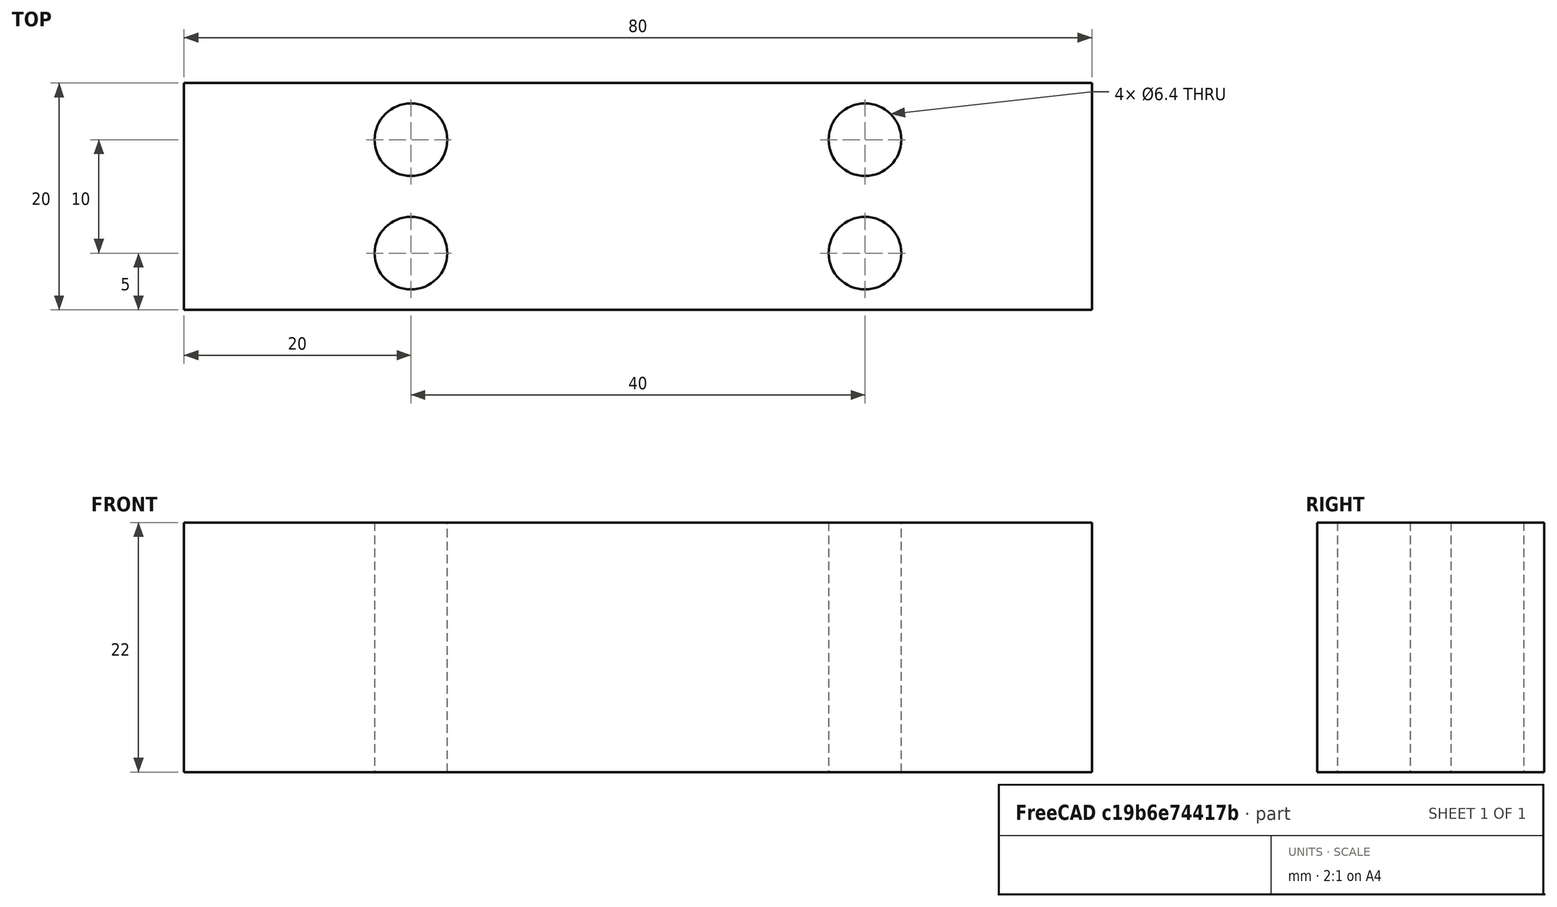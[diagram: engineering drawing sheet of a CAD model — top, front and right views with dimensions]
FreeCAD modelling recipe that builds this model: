
FCSTD DOCUMENT  (FreeCAD 0.18R16110 (Git))
Label: nutblock1b
License: All rights reserved
LicenseURL: http://en.wikipedia.org/wiki/All_rights_reserved
objects: Sketcher::SketchObject×1, PartDesign::Pad×1, PartDesign::Body×1
note: 4 computed .brp shape members not serialized (recipe doc carries the construction recipe); baked Part::Feature solids carry a one-line shape summary decoded from their .brp

FEATURE [Sketcher::SketchObject] Sketch
  MapMode = 5
  Support = -> [XY_Plane]
  sketch-geometry (8):
    g0: LineSegment StartX=0 StartY=20 StartZ=0 EndX=80 EndY=20 EndZ=0
    g1: LineSegment StartX=80 StartY=20 StartZ=0 EndX=80 EndY=0 EndZ=0
    g2: LineSegment StartX=80 StartY=0 StartZ=0 EndX=0 EndY=0 EndZ=0
    g3: LineSegment StartX=0 StartY=0 StartZ=0 EndX=0 EndY=20 EndZ=0
    g4: Circle CenterX=20 CenterY=15 CenterZ=0 NormalX=0 NormalY=0 NormalZ=1 AngleXU=0 Radius=3.2
    g5: Circle CenterX=20 CenterY=5 CenterZ=0 NormalX=0 NormalY=0 NormalZ=1 AngleXU=0 Radius=3.2
    g6: Circle CenterX=60 CenterY=15 CenterZ=0 NormalX=0 NormalY=0 NormalZ=1 AngleXU=0 Radius=3.2
    g7: Circle CenterX=60 CenterY=5 CenterZ=0 NormalX=0 NormalY=0 NormalZ=1 AngleXU=0 Radius=3.2
  constraints (23):
    c: Coincident(g0,g1)
    c: Coincident(g1,g2)
    c: Coincident(g2,g3)
    c: Coincident(g3,g0)
    c: Horizontal(g0)
    c: Horizontal(g2)
    c: Vertical(g1)
    c: Vertical(g3)
    c: DistanceX(g0,g0) = 80
    c: DistanceY(g3,g3) = 20
    c: Coincident(g2,g-1)
    c: DistanceX(g2,g5) = 20
    c: DistanceX(g4,g5) = 0
    c: DistanceX(g4,g6) = 40
    c: DistanceX(g6,g7) = 0
    c: DistanceY(g2,g5) = 5
    c: DistanceY(g5,g4) = 10
    c: DistanceY(g5,g7) = 0
    c: DistanceY(g4,g6) = 0
    c: Radius(g4) = 3.2  'durchgangsloch_m6'
    c: Equal(g4,g6)
    c: Equal(g4,g7)
    c: Equal(g4,g5)
FEATURE [PartDesign::Pad] Pad
  Length = 22
  Length2 = 100
  Profile = -> Sketch
  Type = 0
FEATURE [PartDesign::Body] Body
  Group = -> [Sketch,Pad]
  Origin = -> Origin
  Tip = -> Pad
